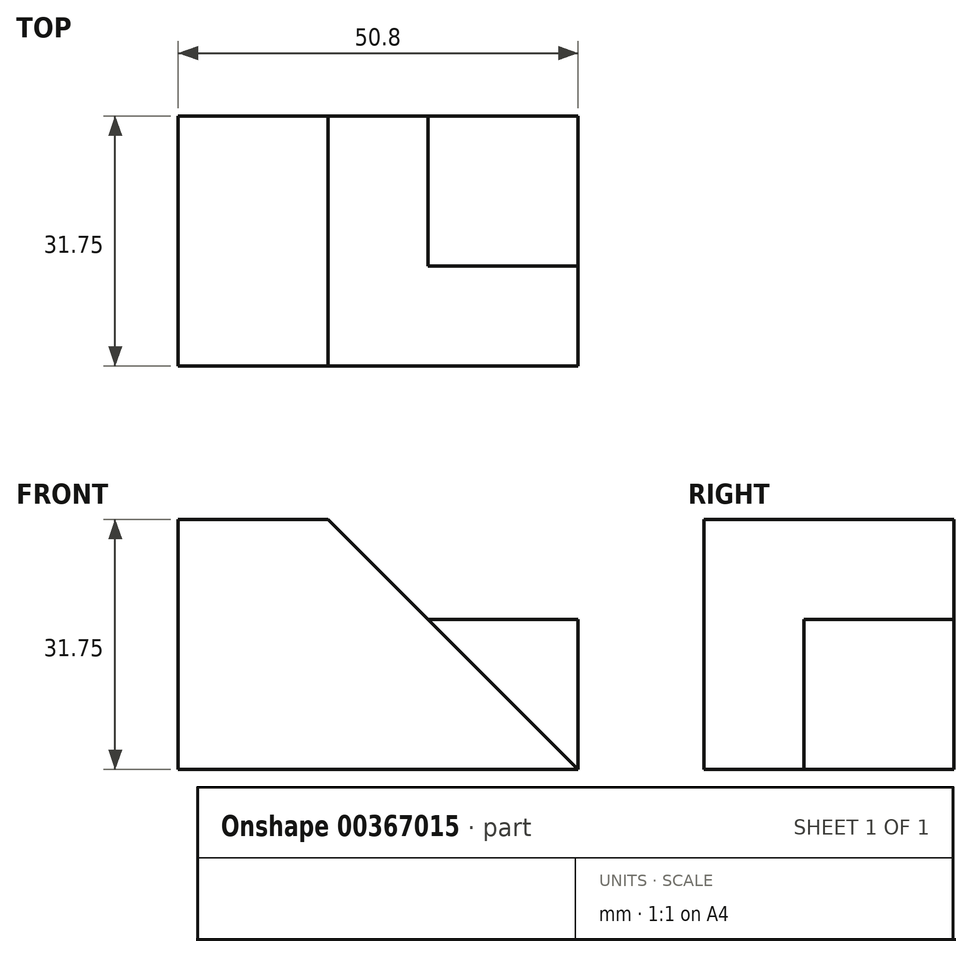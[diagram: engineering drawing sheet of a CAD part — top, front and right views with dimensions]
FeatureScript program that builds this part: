
annotation { "Feature Type Name" : "Feature", "Feature Type Description" : "" }
export const myFeature = defineFeature(function(context is Context, id is Id, definition is map)
    precondition{}
    {
        {
            var Q0;
            Q0=qCreatedBy(makeId("Front.planeOp"),FACE);
            var sketch = newSketch(context, id + "F0", { "sketchPlane" : qUnion([Q0])});
            skLineSegment(sketch, "E0", {"start": v(0, 0) * mm, "end": v(0, 31.75) * mm});
            skLineSegment(sketch, "E1", {"start": v(0, 31.75) * mm, "end": v(50.8, 31.75) * mm});
            skLineSegment(sketch, "E2", {"start": v(50.8, 31.75) * mm, "end": v(50.8, 0) * mm});
            skLineSegment(sketch, "E3", {"start": v(50.8, 0) * mm, "end": v(0, 0) * mm});
            skSolve(sketch);
        }
        {
            var Q0;
            Q0 = qSketchRegion(id + "F0", true);
            extrude(context, id + "F1", {"entities" : qUnion([Q0]), "depth" : 31.75 * mm});
        }
        {
            var Q0;
            Q0=makeQuery(id+"F1.opExtrude","CAP_FACE",FACE,{"disambiguationData":[OSD([sQuery(id+"F0.wireOp",EDGE,"E0"),sQuery(id+"F0.wireOp",EDGE,"E1"),sQuery(id+"F0.wireOp",EDGE,"E2"),sQuery(id+"F0.wireOp",EDGE,"E3")])],"isStart":false});
            var sketch = newSketch(context, id + "F2", { "sketchPlane" : qUnion([Q0])});
            skLineSegment(sketch, "E4", {"start": v(50.8, 0) * mm, "end": v(19.05, 31.75) * mm});
            skSolve(sketch);
        }
        {
            var Q0;
            Q0 = qSketchRegion(id + "F2", true);
            var Q1;
            {var subQ0=sQuery(id+"F2.wireOp",EDGE,"E4");Q1=makeQuery(id+"F2.imprint","IMPRINT",FACE,{"disambiguationData":[TD([[makeQuery(id+"F2.imprint","IMPRINT",EDGE,{"derivedFrom":subQ0}),-1.0]])]});}
            extrude(context, id + "F3", {"entities" : qUnion([Q0, Q1]), "operationType" : NewBodyOperationType.REMOVE, "oppositeDirection" : true, "depth" : 50.8 * mm});
        }
        {
            var Q0;
            Q0=qCreatedBy(makeId("Right.planeOp"),FACE);
            var sketch = newSketch(context, id + "F4", { "sketchPlane" : qUnion([Q0])});
            skLineSegment(sketch, "E5.bottom", {"start": v(0, 0) * mm, "end": v(-19.05, 0) * mm});
            skLineSegment(sketch, "E5.top", {"start": v(0, 19.05) * mm, "end": v(-19.05, 19.05) * mm});
            skLineSegment(sketch, "E5.left", {"start": v(0, 0) * mm, "end": v(0, 19.05) * mm});
            skLineSegment(sketch, "E5.right", {"start": v(-19.05, 0) * mm, "end": v(-19.05, 19.05) * mm});
            skSolve(sketch);
        }
        {
            var Q0;
            Q0 = qSketchRegion(id + "F4", true);
            extrude(context, id + "F5", {"entities" : qUnion([Q0]), "operationType" : NewBodyOperationType.ADD, "depth" : 50.8 * mm});
        }
    });
